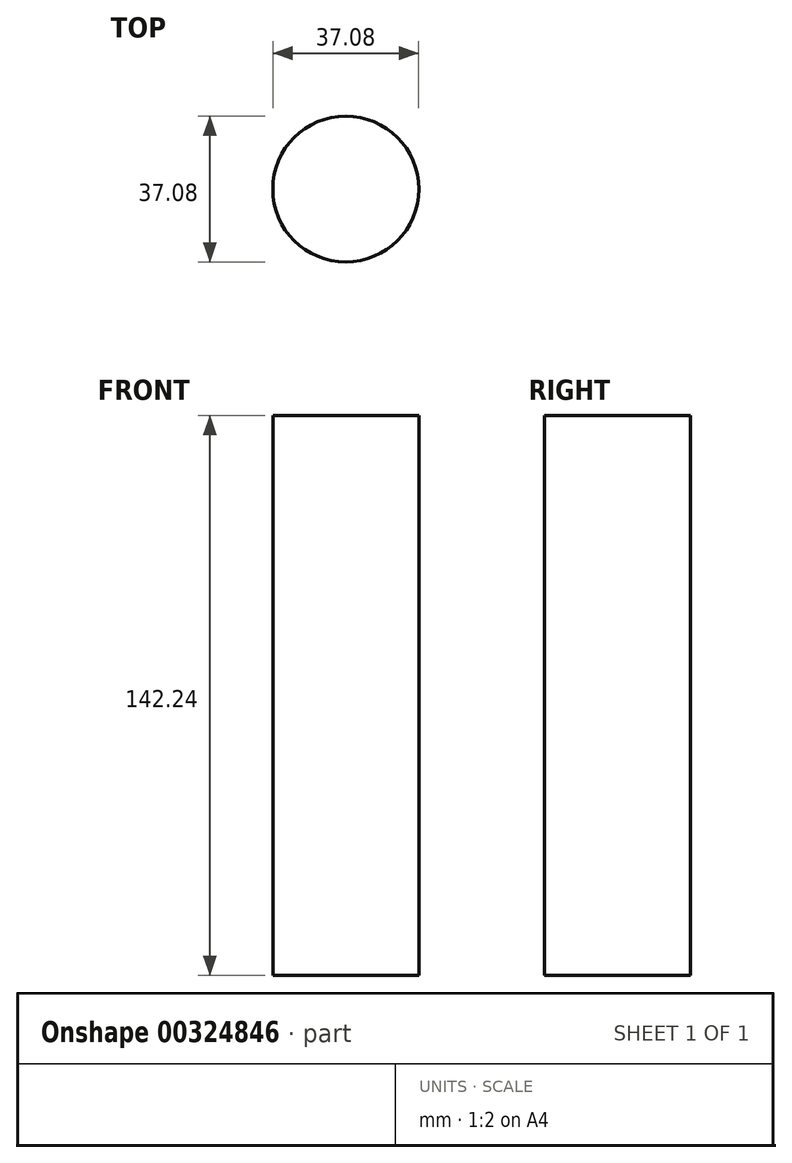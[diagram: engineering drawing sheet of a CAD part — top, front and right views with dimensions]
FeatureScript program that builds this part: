
annotation { "Feature Type Name" : "Feature", "Feature Type Description" : "" }
export const myFeature = defineFeature(function(context is Context, id is Id, definition is map)
    precondition{}
    {
        {
            var Q0;
            Q0=qCreatedBy(makeId("Top.planeOp"),FACE);
            var sketch = newSketch(context, id + "F0", { "sketchPlane" : qUnion([Q0])});
            skCircle(sketch, "E0", {"center": v(0, 0) * mm, "radius": 18.54 * mm});
            skSolve(sketch);
        }
        {
            var Q0;
            Q0 = qSketchRegion(id + "F0", true);
            extrude(context, id + "F1", {"entities" : qUnion([Q0]), "depth" : 142.24 * mm});
        }
    });
